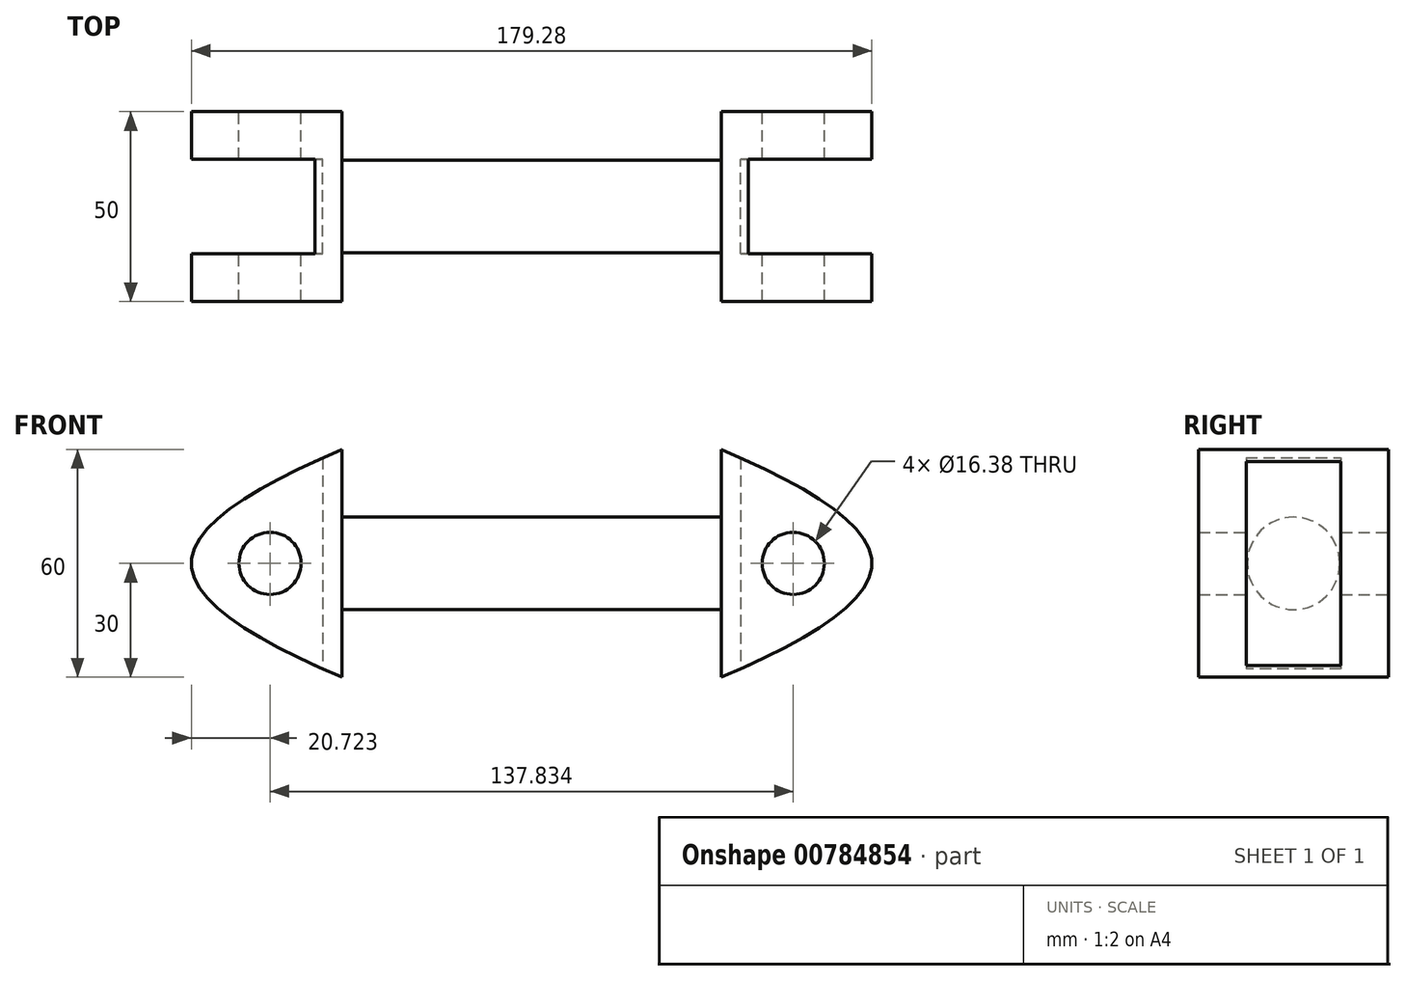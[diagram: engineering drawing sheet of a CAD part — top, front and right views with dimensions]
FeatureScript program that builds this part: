
annotation { "Feature Type Name" : "Feature", "Feature Type Description" : "" }
export const myFeature = defineFeature(function(context is Context, id is Id, definition is map)
    precondition{}
    {
        {
            var Q0;
            Q0=qCreatedBy(makeId("Front.planeOp"),FACE);
            var sketch = newSketch(context, id + "F0", { "sketchPlane" : qUnion([Q0])});
            skLineSegment(sketch, "E0", {"start": v(-50, 12.18) * mm, "end": v(0, 12.18) * mm});
            skLineSegment(sketch, "E1", {"start": v(99.92, 0) * mm, "end": v(50, 0) * mm, "construction": true});
            skLineSegment(sketch, "E2", {"start": v(0, 31.32) * mm, "end": v(0, -30.04) * mm, "construction": true});
            skLineSegment(sketch, "E3.MirrorCS", {"start": v(50, 12.18) * mm, "end": v(0, 12.18) * mm});
            skPoint(sketch, "E4.orphan", {"position": v(-98.14, 0) * mm});
            skLineSegment(sketch, "E5", {"start": v(-50, 12.18) * mm, "end": v(-50, 0) * mm});
            skLineSegment(sketch, "E6", {"start": v(-50, 0) * mm, "end": v(50, 0) * mm});
            skLineSegment(sketch, "E7", {"start": v(50, 12.18) * mm, "end": v(50, 0) * mm});
            skSolve(sketch);
        }
        {
            var Q0;
            Q0=makeQuery(id+"F0.imprint","IMPRINT",FACE,{"disambiguationData":[TD([[makeQuery(id+"F0.imprint","IMPRINT",EDGE,{"derivedFrom":sQuery(id+"F0.wireOp",EDGE,"E0")}),-1.0]])]});
            var Q1;
            Q1=sQuery(id+"F0.wireOp",EDGE,"E1");
            revolve(context, id + "F1", {"surfaceOperationType" : NewSurfaceOperationType.NEW, "entities" : qUnion([Q0]), "axis" : qUnion([Q1]), "revolveType" : RevolveType.FULL});
        }
        {
            var Q0;
            Q0=qCreatedBy(makeId("Front.planeOp"),FACE);
            var sketch = newSketch(context, id + "F2", { "sketchPlane" : qUnion([Q0])});
            skLineSegment(sketch, "E8", {"start": v(-50, 30) * mm, "end": v(-50, -30) * mm});
            skFitSpline(sketch, "E9", {"points": [v(-50, 30) * mm, v(-89.64, 0) * mm, v(-50, -30) * mm], "startDerivative": vector(-141.23, -60) * mm, "endDerivative": vector(141.23, -60) * mm});
            skCircle(sketch, "E10", {"center": v(-68.92, 0) * mm, "radius": 8.19 * mm});
            skLineSegment(sketch, "E11", {"start": v(0, 41) * mm, "end": v(0, -54.76) * mm, "construction": true});
            skLineSegment(sketch, "E12.MirrorCS", {"start": v(50, 30) * mm, "end": v(50, -30) * mm});
            skFitSpline(sketch, "E13.MirrorCS", {"points": [v(50, 30) * mm, v(89.64, 0) * mm, v(50, -30) * mm], "startDerivative": vector(141.23, -60) * mm, "endDerivative": vector(-141.23, -60) * mm});
            skCircle(sketch, "E14.MirrorC", {"center": v(68.92, 0) * mm, "radius": 8.19 * mm});
            skSolve(sketch);
        }
        {
            var Q0;
            Q0 = qSketchRegion(id + "F2", true);
            extrude(context, id + "F3", {"entities" : qUnion([Q0]), "operationType" : NewBodyOperationType.ADD, "endBound" : BoundingType.SYMMETRIC, "depth" : 50 * mm, "offsetDistance" : 25 * mm});
        }
        {
            var Q0;
            Q0=qCreatedBy(makeId("Front.planeOp"),FACE);
            var sketch = newSketch(context, id + "F4", { "sketchPlane" : qUnion([Q0])});
            skLineSegment(sketch, "E15.0", {"start": v(-55, 27.82) * mm, "end": v(-55, -27.82) * mm});
            skFitSpline(sketch, "E16.0", {"points": [v(-50, 30) * mm, v(-73.54, 20) * mm, v(-105.74, 0) * mm, v(-73.54, -20) * mm, v(-50, -30) * mm]});
            skLineSegment(sketch, "E17", {"start": v(0, 33.3) * mm, "end": v(0, -38.63) * mm, "construction": true});
            skLineSegment(sketch, "E18.MirrorCS", {"start": v(55, 27.82) * mm, "end": v(55, -27.82) * mm});
            skFitSpline(sketch, "E19.0", {"points": [v(50, 30) * mm, v(73.54, 20) * mm, v(105.74, 0) * mm, v(73.54, -20) * mm, v(50, -30) * mm]});
            skSolve(sketch);
        }
        {
            var Q0;
            Q0 = qSketchRegion(id + "F4", true);
            extrude(context, id + "F5", {"entities" : qUnion([Q0]), "operationType" : NewBodyOperationType.REMOVE, "endBound" : BoundingType.SYMMETRIC, "depth" : 25 * mm, "offsetDistance" : 25 * mm});
        }
    });
